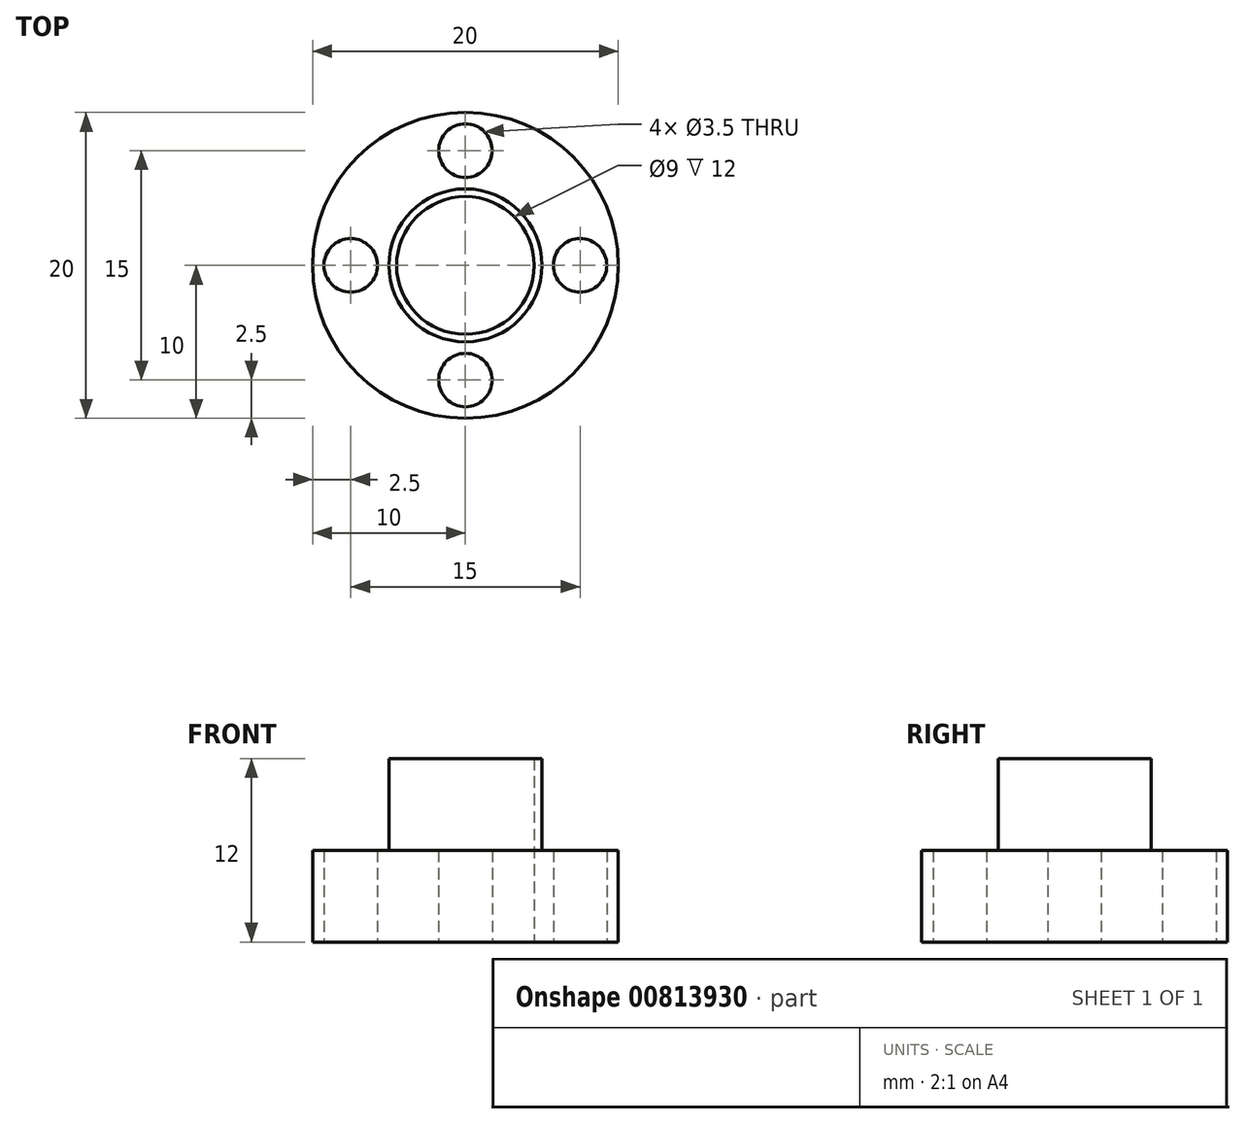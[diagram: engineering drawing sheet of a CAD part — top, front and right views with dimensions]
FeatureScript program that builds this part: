
annotation { "Feature Type Name" : "Feature", "Feature Type Description" : "" }
export const myFeature = defineFeature(function(context is Context, id is Id, definition is map)
    precondition{}
    {
        {
            var Q0;
            Q0=qCreatedBy(makeId("Top.planeOp"),FACE);
            var sketch = newSketch(context, id + "F0", { "sketchPlane" : qUnion([Q0])});
            skCircle(sketch, "E0", {"center": v(0, 0) * mm, "radius": 5 * mm});
            skCircle(sketch, "E1", {"center": v(0, 7.5) * mm, "radius": 1.75 * mm});
            skCircle(sketch, "E2", {"center": v(0, 0) * mm, "radius": 4.5 * mm});
            skCircle(sketch, "E3.1.0", {"center": v(-7.5, 0) * mm, "radius": 1.75 * mm});
            skCircle(sketch, "E3.2.0", {"center": v(0, -7.5) * mm, "radius": 1.75 * mm});
            skCircle(sketch, "E3.3.0", {"center": v(7.5, 0) * mm, "radius": 1.75 * mm});
            skSolve(sketch);
        }
        {
            var Q0;
            Q0=qCreatedBy(makeId("Top.planeOp"),FACE);
            var sketch = newSketch(context, id + "F1", { "sketchPlane" : qUnion([Q0])});
            skCircle(sketch, "E4", {"center": v(0, 0) * mm, "radius": 10 * mm});
            skSolve(sketch);
        }
        {
            var Q0;
            Q0=makeQuery(id+"F1.imprint","IMPRINT",FACE,{"disambiguationData":[TD([[makeQuery(id+"F1.imprint","IMPRINT",EDGE,{"derivedFrom":sQuery(id+"F1.wireOp",EDGE,"E4")}),1.0]])]});
            extrude(context, id + "F2", {"entities" : qUnion([Q0]), "depth" : 6 * mm, "offsetDistance" : 25 * mm});
        }
        {
            var Q0;
            Q0 = qSketchRegion(id + "F0", true);
            extrude(context, id + "F3", {"entities" : qUnion([Q0]), "operationType" : NewBodyOperationType.REMOVE, "endBound" : BoundingType.SYMMETRIC, "depth" : 12 * mm, "offsetDistance" : 25 * mm});
        }
        {
            var Q0;
            Q0=makeQuery(id+"F3.boolean.opBoolean","SPLIT",FACE,{"disambiguationData":[TD([makeQuery(id+"F3.opExtrude","SWEPT_FACE",FACE,{"disambiguationData":[OSD([sQuery(id+"F0.wireOp",EDGE,"E2")])]})])],"derivedFrom":makeQuery(id+"F2.opExtrude","CAP_FACE",FACE,{"disambiguationData":[OSD([sQuery(id+"F1.wireOp",EDGE,"E4")])],"isStart":false})});
            extrude(context, id + "F4", {"entities" : qUnion([Q0]), "operationType" : NewBodyOperationType.REMOVE, "oppositeDirection" : true, "depth" : 6 * mm, "offsetDistance" : 25 * mm});
        }
        {
            var Q0;
            Q0=sQuery(id+"F0.wireOp",EDGE,"E0");
            extrude(context, id + "F5", {"bodyType" : ToolBodyType.SURFACE, "surfaceEntities" : qUnion([Q0]), "depth" : 12 * mm, "offsetDistance" : 25 * mm});
        }
        {
            var Q0;
            Q0=sQuery(id+"F0.wireOp",EDGE,"E0");
            extrude(context, id + "F6", {"bodyType" : ToolBodyType.SURFACE, "surfaceOperationType" : NewSurfaceOperationType.ADD, "surfaceEntities" : qUnion([Q0]), "depth" : 12 * mm, "offsetDistance" : 25 * mm});
        }
        {
            var Q0;
            Q0=makeQuery(id+"F0.imprint","IMPRINT",FACE,{"disambiguationData":[TD([[makeQuery(id+"F0.imprint","IMPRINT",EDGE,{"derivedFrom":sQuery(id+"F0.wireOp",EDGE,"E0")}),1.0]])]});
            extrude(context, id + "F7", {"entities" : qUnion([Q0]), "operationType" : NewBodyOperationType.ADD, "depth" : 12 * mm, "offsetDistance" : 25 * mm});
        }
    });
